# Revit family: Faucet-Lavatory-KOHLER-Aleo-K-72312ME
name_source: partatom
category: Plumbing Fixtures
units: mm (PartAtom-declared; Revit-internal decimal feet)

## family parameters
Cut with Voids When Loaded = No
Host = Face
Maintain Annotation Orientation = No
Part Type = Normal
Room Calculation Point = No
Round Connector Dimension = Use Diameter
Shared = No

## types (3) — shared parameters
ADA Compliant = No
Assembly Code = D2010
CW Connection = Yes
Cold Water Inlet = Cold Water Inlet
Date Modified = 06/29/2025
Default Elevation = 36"
HW Connection = Yes
Handle Clearance = 3 13/16"
Height = 5 5/8"
Hot Water Inlet = Hot Water Inlet
Length = 4 1/8"
Manufacturer = Kohler Co.
Master Format 2014 = 22 41 39
Master Format 2014 Name = Residential Faucets, Supplies, and Trim
Material = Premium Metal Construction
Pressure = 0.00 psi
Product Name = Aleo
Spout Reach = 4 1/8"
URL = https://me.kohler.com
Vent Connection = No
Waste Connection = No
Waste Water Outlet = Waste Water Outlet
WaterSense Certified = No
Width = 2"

## per-type parameters (varying)
| type | 4 | Description | Drain Included | Finish | Flow Rate | Model | Type |
| AF-Vibrant French Gold | No | Lavatory Faucet Without Drain | No | Kohler-Metal-AF-Vibrant_French_Gold | 1 GPM | K-72312ME-4ND-AF | 1 |
| BL-Matte Black | No | Lavatory Faucet Without Drain | No | Kohler-Metal-BL-Matte_Black | 2 GPM | K-72312ME-4ND-BL | 2 |
| BV-Brushed Bronze | Yes | Lavatory Faucet With Drain | Yes | Kohler-Metal-BV-Brushed_Bronze | 1 GPM | K-72312ME-4-BV | 3 |

## geometry (parser evidence)
native form markers: Sweep x5
no freeform markers — native parametric forms only
